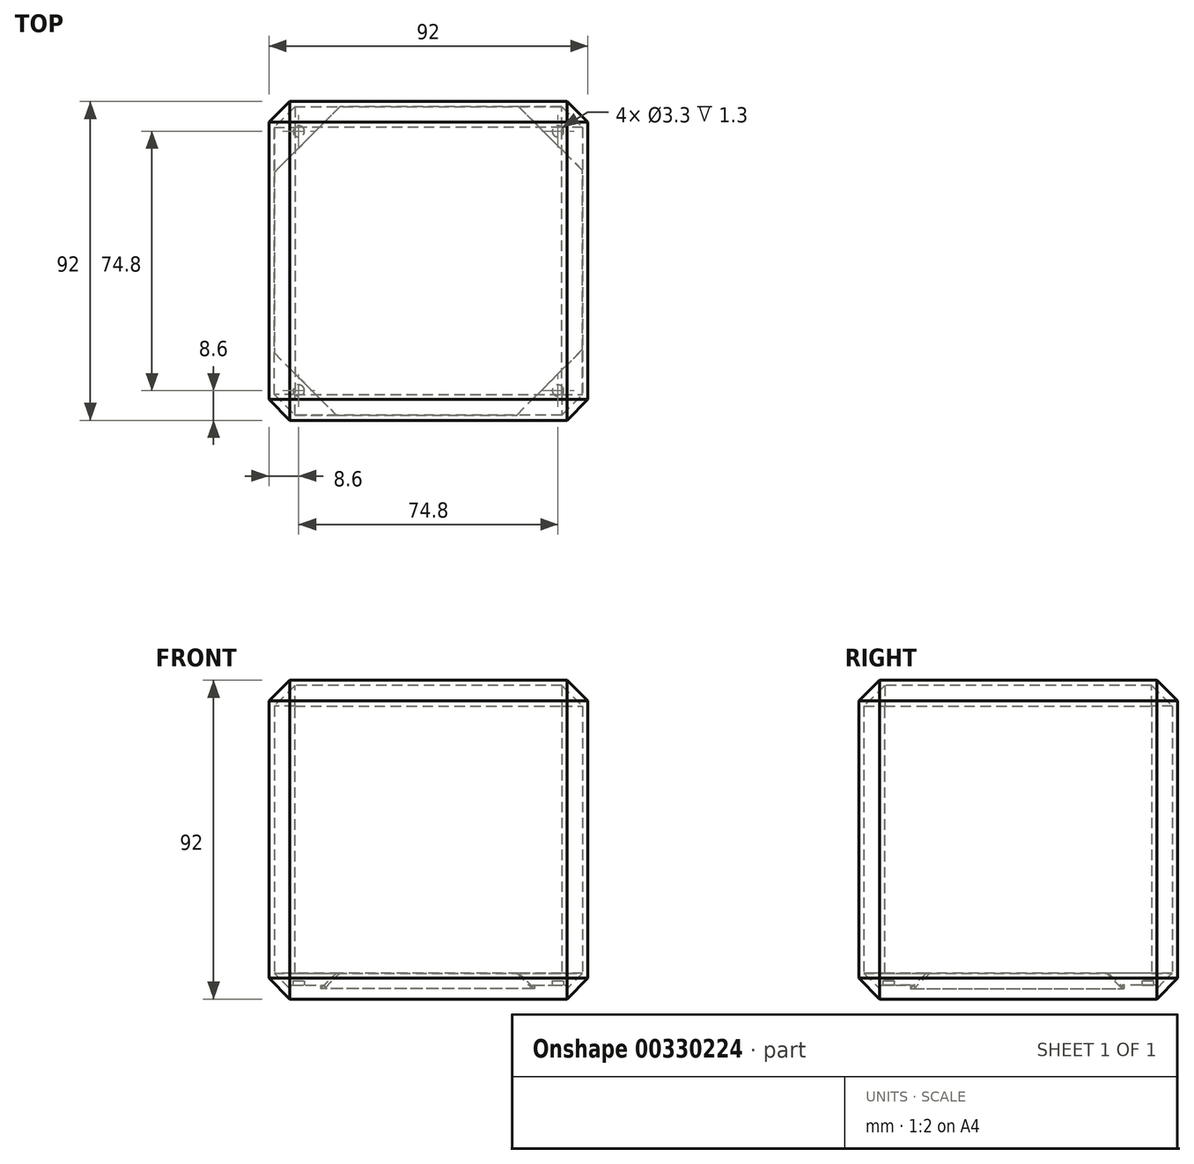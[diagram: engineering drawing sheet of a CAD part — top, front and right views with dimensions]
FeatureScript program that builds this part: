
annotation { "Feature Type Name" : "Feature", "Feature Type Description" : "" }
export const myFeature = defineFeature(function(context is Context, id is Id, definition is map)
    precondition{}
    {
        {
            var Q0;
            Q0=qCreatedBy(makeId("Top.planeOp"),FACE);
            var sketch = newSketch(context, id + "F0", { "sketchPlane" : qUnion([Q0])});
            skLineSegment(sketch, "E0.bottom", {"start": v(46, -46) * mm, "end": v(-46, -46) * mm});
            skLineSegment(sketch, "E0.top", {"start": v(46, 46) * mm, "end": v(-46, 46) * mm});
            skLineSegment(sketch, "E0.left", {"start": v(46, -46) * mm, "end": v(46, 46) * mm});
            skLineSegment(sketch, "E0.right", {"start": v(-46, -46) * mm, "end": v(-46, 46) * mm});
            skSolve(sketch);
        }
        {
            var Q0;
            Q0=qSketchRegion(id+"F0",true);
            extrude(context, id + "F1", {"entities" : qUnion([Q0]), "depth" : 92 * mm});
        }
        {
            var Q0;
            Q0=makeQuery(id+"F1.opExtrude","CAP_EDGE",EDGE,{"disambiguationData":[OSD([sQuery(id+"F0.wireOp",EDGE,"E0.bottom")])],"isStart":false});
            var Q1;
            Q1=makeQuery(id+"F1.opExtrude","CAP_EDGE",EDGE,{"disambiguationData":[OSD([sQuery(id+"F0.wireOp",EDGE,"E0.left")])],"isStart":false});
            var Q2;
            Q2=makeQuery(id+"F1.opExtrude","SWEPT_EDGE",EDGE,{"disambiguationData":[OSD([sQuery(id+"F0.wireOp",EDGE,"E0.bottom"),sQuery(id+"F0.wireOp",EDGE,"E0.left")])]});
            var Q3;
            Q3=makeQuery(id+"F1.opExtrude","CAP_EDGE",EDGE,{"disambiguationData":[OSD([sQuery(id+"F0.wireOp",EDGE,"E0.bottom")])],"isStart":true});
            var Q4;
            Q4=makeQuery(id+"F1.opExtrude","SWEPT_EDGE",EDGE,{"disambiguationData":[OSD([sQuery(id+"F0.wireOp",EDGE,"E0.bottom"),sQuery(id+"F0.wireOp",EDGE,"E0.right")])]});
            var Q5;
            Q5=makeQuery(id+"F1.opExtrude","CAP_EDGE",EDGE,{"disambiguationData":[OSD([sQuery(id+"F0.wireOp",EDGE,"E0.left")])],"isStart":true});
            var Q6;
            Q6=makeQuery(id+"F1.opExtrude","SWEPT_EDGE",EDGE,{"disambiguationData":[OSD([sQuery(id+"F0.wireOp",EDGE,"E0.top"),sQuery(id+"F0.wireOp",EDGE,"E0.left")])]});
            var Q7;
            Q7=makeQuery(id+"F1.opExtrude","CAP_EDGE",EDGE,{"disambiguationData":[OSD([sQuery(id+"F0.wireOp",EDGE,"E0.top")])],"isStart":false});
            var Q8;
            Q8=makeQuery(id+"F1.opExtrude","CAP_EDGE",EDGE,{"disambiguationData":[OSD([sQuery(id+"F0.wireOp",EDGE,"E0.right")])],"isStart":false});
            var Q9;
            Q9=makeQuery(id+"F1.opExtrude","CAP_EDGE",EDGE,{"disambiguationData":[OSD([sQuery(id+"F0.wireOp",EDGE,"E0.right")])],"isStart":true});
            var Q10;
            Q10=makeQuery(id+"F1.opExtrude","SWEPT_EDGE",EDGE,{"disambiguationData":[OSD([sQuery(id+"F0.wireOp",EDGE,"E0.top"),sQuery(id+"F0.wireOp",EDGE,"E0.right")])]});
            var Q11;
            Q11=makeQuery(id+"F1.opExtrude","CAP_EDGE",EDGE,{"disambiguationData":[OSD([sQuery(id+"F0.wireOp",EDGE,"E0.top")])],"isStart":true});
            chamfer(context, id + "F2", {"entities" : qUnion([Q0, Q1, Q2, Q3, Q4, Q5, Q6, Q7, Q8, Q9, Q10, Q11]), "width" : 6 * mm, "tangentPropagation" : true});
        }
        {
            var Q0;
            Q0=makeQuery(id+"F1.opExtrude","CAP_FACE",FACE,{"disambiguationData":[OSD([sQuery(id+"F0.wireOp",EDGE,"E0.bottom"),sQuery(id+"F0.wireOp",EDGE,"E0.top"),sQuery(id+"F0.wireOp",EDGE,"E0.left"),sQuery(id+"F0.wireOp",EDGE,"E0.right")])],"isStart":true});
            extrude(context, id + "F3", {"entities" : qUnion([Q0]), "operationType" : NewBodyOperationType.REMOVE, "oppositeDirection" : true, "depth" : 80 * mm});
        }
        {
            var Q0;
            Q0=qCreatedBy(makeId("Top.planeOp"),FACE);
            var sketch = newSketch(context, id + "F4", { "sketchPlane" : qUnion([Q0])});
            skLineSegment(sketch, "E1.bottom", {"start": v(-44.5, 44.5) * mm, "end": v(44.5, 44.5) * mm});
            skLineSegment(sketch, "E1.top", {"start": v(-44.5, -44.5) * mm, "end": v(44.5, -44.5) * mm});
            skLineSegment(sketch, "E1.left", {"start": v(-44.5, 44.5) * mm, "end": v(-44.5, -44.5) * mm});
            skLineSegment(sketch, "E1.right", {"start": v(44.5, 44.5) * mm, "end": v(44.5, -44.5) * mm});
            skSolve(sketch);
        }
        {
            var Q0;
            Q0=qSketchRegion(id+"F4",true);
            extrude(context, id + "F5", {"entities" : qUnion([Q0]), "depth" : 89 * mm});
        }
        {
            var Q0;
            Q0=makeQuery(id+"F5.opExtrude","SWEPT_EDGE",EDGE,{"disambiguationData":[OSD([sQuery(id+"F4.wireOp",EDGE,"E1.top"),sQuery(id+"F4.wireOp",EDGE,"E1.left")])]});
            var Q1;
            Q1=makeQuery(id+"F5.opExtrude","CAP_EDGE",EDGE,{"disambiguationData":[OSD([sQuery(id+"F4.wireOp",EDGE,"E1.top")])],"isStart":false});
            var Q2;
            Q2=makeQuery(id+"F5.opExtrude","SWEPT_EDGE",EDGE,{"disambiguationData":[OSD([sQuery(id+"F4.wireOp",EDGE,"E1.top"),sQuery(id+"F4.wireOp",EDGE,"E1.right")])]});
            var Q3;
            Q3=makeQuery(id+"F5.opExtrude","CAP_EDGE",EDGE,{"disambiguationData":[OSD([sQuery(id+"F4.wireOp",EDGE,"E1.top")])],"isStart":true});
            var Q4;
            Q4=makeQuery(id+"F5.opExtrude","CAP_EDGE",EDGE,{"disambiguationData":[OSD([sQuery(id+"F4.wireOp",EDGE,"E1.right")])],"isStart":false});
            var Q5;
            Q5=makeQuery(id+"F5.opExtrude","SWEPT_EDGE",EDGE,{"disambiguationData":[OSD([sQuery(id+"F4.wireOp",EDGE,"E1.bottom"),sQuery(id+"F4.wireOp",EDGE,"E1.right")])]});
            var Q6;
            Q6=makeQuery(id+"F5.opExtrude","CAP_EDGE",EDGE,{"disambiguationData":[OSD([sQuery(id+"F4.wireOp",EDGE,"E1.right")])],"isStart":true});
            var Q7;
            Q7=makeQuery(id+"F5.opExtrude","CAP_EDGE",EDGE,{"disambiguationData":[OSD([sQuery(id+"F4.wireOp",EDGE,"E1.bottom")])],"isStart":true});
            var Q8;
            Q8=makeQuery(id+"F5.opExtrude","CAP_EDGE",EDGE,{"disambiguationData":[OSD([sQuery(id+"F4.wireOp",EDGE,"E1.left")])],"isStart":false});
            var Q9;
            Q9=makeQuery(id+"F5.opExtrude","CAP_EDGE",EDGE,{"disambiguationData":[OSD([sQuery(id+"F4.wireOp",EDGE,"E1.bottom")])],"isStart":false});
            var Q10;
            Q10=makeQuery(id+"F5.opExtrude","SWEPT_EDGE",EDGE,{"disambiguationData":[OSD([sQuery(id+"F4.wireOp",EDGE,"E1.bottom"),sQuery(id+"F4.wireOp",EDGE,"E1.left")])]});
            var Q11;
            Q11=makeQuery(id+"F5.opExtrude","CAP_EDGE",EDGE,{"disambiguationData":[OSD([sQuery(id+"F4.wireOp",EDGE,"E1.left")])],"isStart":true});
            chamfer(context, id + "F6", {"entities" : qUnion([Q0, Q1, Q2, Q3, Q4, Q5, Q6, Q7, Q8, Q9, Q10, Q11]), "width" : 6 * mm, "tangentPropagation" : true});
        }
        {
            var Q0;
            Q0=makeQuery(id+"F5.opExtrude","SWEPT_BODY",BODY,{"disambiguationData":[OSD([sQuery(id+"F4.wireOp",EDGE,"E1.bottom"),sQuery(id+"F4.wireOp",EDGE,"E1.top"),sQuery(id+"F4.wireOp",EDGE,"E1.left"),sQuery(id+"F4.wireOp",EDGE,"E1.right")])]});
            transform(context, id + "F7", {"entities" : qUnion([Q0]), "transformType" : TransformType.TRANSLATION_3D, "dx" : 0 * mm, "dy" : 0 * mm, "dz" : 1.5 * mm, "makeCopy" : false});
        }
        {
            var Q0;
            Q0=makeQuery(id+"F5.opExtrude","SWEPT_BODY",BODY,{"disambiguationData":[OSD([sQuery(id+"F4.wireOp",EDGE,"E1.bottom"),sQuery(id+"F4.wireOp",EDGE,"E1.top"),sQuery(id+"F4.wireOp",EDGE,"E1.left"),sQuery(id+"F4.wireOp",EDGE,"E1.right")])]});
            var Q1;
            Q1=makeQuery(id+"F1.opExtrude","SWEPT_BODY",BODY,{"disambiguationData":[OSD([sQuery(id+"F0.wireOp",EDGE,"E0.bottom"),sQuery(id+"F0.wireOp",EDGE,"E0.top"),sQuery(id+"F0.wireOp",EDGE,"E0.left"),sQuery(id+"F0.wireOp",EDGE,"E0.right")])]});
            booleanBodies(context, id + "F8", {"operationType" : BooleanOperationType.SUBTRACTION, "tools" : qUnion([Q0]), "targets" : qUnion([Q1])});
        }
        {
            var Q0;
            Q0=qCreatedBy(makeId("Top.planeOp"),FACE);
            cPlane(context, id + "F9", {"entities" : qUnion([Q0]), "cplaneType" : CPlaneType.OFFSET, "offset" : 7.5 * mm, "width" : 150 * mm, "height" : 150 * mm});
        }
        {
            var Q0;
            Q0=qCreatedBy(id+"F9.planeOp",FACE);
            var sketch = newSketch(context, id + "F16", { "sketchPlane" : qUnion([Q0])});
            skLineSegment(sketch, "E2.0", {"start": v(44.5, 38.5) * mm, "end": v(44.5, 26.07) * mm});
            skLineSegment(sketch, "E2.1", {"start": v(38.5, 44.5) * mm, "end": v(44.5, 38.5) * mm});
            skLineSegment(sketch, "E2.2", {"start": v(-38.5, 44.5) * mm, "end": v(-25.5, 44.5) * mm});
            skLineSegment(sketch, "E2.3", {"start": v(38.5, -44.5) * mm, "end": v(25.5, -44.5) * mm});
            skLineSegment(sketch, "E2.4", {"start": v(44.5, -38.5) * mm, "end": v(38.5, -44.5) * mm});
            skLineSegment(sketch, "E2.5", {"start": v(-38.5, -44.5) * mm, "end": v(-44.5, -38.5) * mm});
            skLineSegment(sketch, "E2.6", {"start": v(-44.5, -38.5) * mm, "end": v(-44.5, -26.54) * mm});
            skLineSegment(sketch, "E2.7", {"start": v(-44.5, 38.5) * mm, "end": v(-38.5, 44.5) * mm});
            skPoint(sketch, "E3.0.end.orphan", {"position": v(40, 40) * mm});
            skPoint(sketch, "E4.0.end.orphan", {"position": v(-40, 40) * mm});
            skPoint(sketch, "E5.0.end.orphan", {"position": v(-40, -40) * mm});
            skPoint(sketch, "E5.0.start.orphan", {"position": v(40, -40) * mm});
            skLineSegment(sketch, "E6", {"start": v(30, -40) * mm, "end": v(40, -30) * mm});
            skLineSegment(sketch, "E7.MirrorCS", {"start": v(-30, -41.04) * mm, "end": v(-40, -31.04) * mm});
            skLineSegment(sketch, "E8.MirrorCS", {"start": v(30.57, 40) * mm, "end": v(40.57, 30) * mm});
            skLineSegment(sketch, "E9.MirrorCS", {"start": v(-30, 40) * mm, "end": v(-40, 30) * mm});
            skLineSegment(sketch, "E10", {"start": v(40, -30) * mm, "end": v(44.5, -25.5) * mm});
            skLineSegment(sketch, "E11", {"start": v(30, -40) * mm, "end": v(25.5, -44.5) * mm});
            skLineSegment(sketch, "E12", {"start": v(-30, -41.04) * mm, "end": v(-26.54, -44.5) * mm});
            skLineSegment(sketch, "E13", {"start": v(-40, -31.04) * mm, "end": v(-44.5, -26.54) * mm});
            skLineSegment(sketch, "E14", {"start": v(-40, 30) * mm, "end": v(-44.5, 25.5) * mm});
            skLineSegment(sketch, "E15", {"start": v(-30, 40) * mm, "end": v(-25.5, 44.5) * mm});
            skLineSegment(sketch, "E16", {"start": v(30.57, 40) * mm, "end": v(26.07, 44.5) * mm});
            skLineSegment(sketch, "E17", {"start": v(40.57, 30) * mm, "end": v(44.5, 26.07) * mm});
            skLineSegment(sketch, "E18.trimOffspring", {"start": v(44.5, -25.5) * mm, "end": v(44.5, -38.5) * mm});
            skLineSegment(sketch, "E19.trimOffspring", {"start": v(26.07, 44.5) * mm, "end": v(38.5, 44.5) * mm});
            skLineSegment(sketch, "E20.trimOffspring", {"start": v(-44.5, 25.5) * mm, "end": v(-44.5, 38.5) * mm});
            skLineSegment(sketch, "E21.trimOffspring", {"start": v(-26.54, -44.5) * mm, "end": v(-38.5, -44.5) * mm});
            skSolve(sketch);
        }
        {
            var Q0;
            Q0=qSketchRegion(id+"F16",true);
            extrude(context, id + "F17", {"entities" : qUnion([Q0]), "operationType" : NewBodyOperationType.ADD, "oppositeDirection" : true, "depth" : 3.5 * mm});
        }
        {
            var Q0;
            Q0=makeQuery(id+"F17.opExtrude","CAP_FACE",FACE,{"disambiguationData":[OSD([sQuery(id+"F16.wireOp",EDGE,"E2.5"),sQuery(id+"F16.wireOp",EDGE,"E2.6"),sQuery(id+"F16.wireOp",EDGE,"E7.MirrorCS"),sQuery(id+"F16.wireOp",EDGE,"E12"),sQuery(id+"F16.wireOp",EDGE,"E13"),sQuery(id+"F16.wireOp",EDGE,"E21.trimOffspring")])],"isStart":false});
            var sketch = newSketch(context, id + "F10", { "sketchPlane" : qUnion([Q0])});
            skCircle(sketch, "E22", {"center": v(37.4, 37.4) * mm, "radius": 1.65 * mm});
            skCircle(sketch, "E23.MirrorC", {"center": v(-37.4, 37.4) * mm, "radius": 1.65 * mm});
            skCircle(sketch, "E24.MirrorC", {"center": v(-37.4, -37.4) * mm, "radius": 1.65 * mm});
            skCircle(sketch, "E25.MirrorC", {"center": v(37.4, -37.4) * mm, "radius": 1.65 * mm});
            skSolve(sketch);
        }
        {
            var Q0;
            Q0=qSketchRegion(id+"F10",true);
            extrude(context, id + "F11", {"entities" : qUnion([Q0]), "operationType" : NewBodyOperationType.REMOVE, "oppositeDirection" : true, "depth" : 1.3 * mm});
        }
        {
            var Q0;
            Q0=makeQuery(id+"F17.opExtrude","CAP_EDGE",EDGE,{"disambiguationData":[OSD([sQuery(id+"F16.wireOp",EDGE,"E2.2")])],"isStart":false});
            var Q1;
            Q1=makeQuery(id+"F17.opExtrude","CAP_EDGE",EDGE,{"disambiguationData":[OSD([sQuery(id+"F16.wireOp",EDGE,"E20.trimOffspring")])],"isStart":false});
            var Q2;
            Q2=makeQuery(id+"F17.opExtrude","CAP_EDGE",EDGE,{"disambiguationData":[OSD([sQuery(id+"F16.wireOp",EDGE,"E19.trimOffspring")])],"isStart":false});
            var Q3;
            Q3=makeQuery(id+"F17.opExtrude","CAP_EDGE",EDGE,{"disambiguationData":[OSD([sQuery(id+"F16.wireOp",EDGE,"E2.0")])],"isStart":false});
            var Q4;
            Q4=makeQuery(id+"F17.opExtrude","CAP_EDGE",EDGE,{"disambiguationData":[OSD([sQuery(id+"F16.wireOp",EDGE,"E18.trimOffspring")])],"isStart":false});
            var Q5;
            Q5=makeQuery(id+"F17.opExtrude","CAP_EDGE",EDGE,{"disambiguationData":[OSD([sQuery(id+"F16.wireOp",EDGE,"E21.trimOffspring")])],"isStart":false});
            var Q6;
            Q6=makeQuery(id+"F17.opExtrude","CAP_EDGE",EDGE,{"disambiguationData":[OSD([sQuery(id+"F16.wireOp",EDGE,"E2.6")])],"isStart":false});
            var Q7;
            Q7=makeQuery(id+"F17.opExtrude","CAP_EDGE",EDGE,{"disambiguationData":[OSD([sQuery(id+"F16.wireOp",EDGE,"E2.3")])],"isStart":false});
            chamfer(context, id + "F12", {"entities" : qUnion([Q0, Q1, Q2, Q3, Q4, Q5, Q6, Q7]), "width" : 0.5 * mm, "tangentPropagation" : true});
        }
        {
            var Q0;
            {var subQ0=sQuery(id+"F4.wireOp",EDGE,"E1.top");var subQ1=sQuery(id+"F0.wireOp",EDGE,"E0.right");var subQ2=sQuery(id+"F0.wireOp",EDGE,"E0.left");var subQ3=sQuery(id+"F0.wireOp",EDGE,"E0.top");var subQ4=sQuery(id+"F0.wireOp",EDGE,"E0.bottom");Q0=makeQuery(id+"F8.opBoolean","INTERSECT",EDGE,{"derivedFrom":[makeQuery(id+"F3.boolean.opBoolean","COPY",FACE,{"derivedFrom":makeQuery(id+"F3.opExtrude","SWEPT_FACE",FACE,{"disambiguationData":[OSD([subQ4,subQ3,subQ2,subQ1]),TDD([makeQuery(id+"F2.opChamfer","BLEND_EDGE",EDGE,{"blendedFrom":[makeQuery(id+"F1.opExtrude","CAP_EDGE",EDGE,{"disambiguationData":[OSD([subQ4])],"isStart":true}),makeQuery(id+"F1.opExtrude","CAP_FACE",FACE,{"disambiguationData":[OSD([subQ4,subQ3,subQ2,subQ1])],"isStart":true})],"blendedInto":[makeQuery(id+"F1.opExtrude","CAP_FACE",FACE,{"disambiguationData":[OSD([subQ4,subQ3,subQ2,subQ1])],"isStart":true})]})])]})}),makeQuery(id+"F6.opChamfer","BLEND_FACE",FACE,{"disambiguationData":[OSD([subQ0]),TDD([makeQuery(id+"F5.opExtrude","CAP_EDGE",EDGE,{"disambiguationData":[OSD([subQ0])],"isStart":true})])]})]});}
            var Q1;
            {var subQ0=sQuery(id+"F4.wireOp",EDGE,"E1.bottom");var subQ1=sQuery(id+"F0.wireOp",EDGE,"E0.right");var subQ2=sQuery(id+"F0.wireOp",EDGE,"E0.left");var subQ3=sQuery(id+"F0.wireOp",EDGE,"E0.top");var subQ4=sQuery(id+"F0.wireOp",EDGE,"E0.bottom");Q1=makeQuery(id+"F8.opBoolean","INTERSECT",EDGE,{"derivedFrom":[makeQuery(id+"F3.boolean.opBoolean","COPY",FACE,{"derivedFrom":makeQuery(id+"F3.opExtrude","SWEPT_FACE",FACE,{"disambiguationData":[OSD([subQ4,subQ3,subQ2,subQ1]),TDD([makeQuery(id+"F2.opChamfer","BLEND_EDGE",EDGE,{"blendedFrom":[makeQuery(id+"F1.opExtrude","CAP_EDGE",EDGE,{"disambiguationData":[OSD([subQ3])],"isStart":true}),makeQuery(id+"F1.opExtrude","CAP_FACE",FACE,{"disambiguationData":[OSD([subQ4,subQ3,subQ2,subQ1])],"isStart":true})],"blendedInto":[makeQuery(id+"F1.opExtrude","CAP_FACE",FACE,{"disambiguationData":[OSD([subQ4,subQ3,subQ2,subQ1])],"isStart":true})]})])]})}),makeQuery(id+"F6.opChamfer","BLEND_FACE",FACE,{"disambiguationData":[OSD([subQ0]),TDD([makeQuery(id+"F5.opExtrude","CAP_EDGE",EDGE,{"disambiguationData":[OSD([subQ0])],"isStart":true})])]})]});}
            cPlane(context, id + "F13", {"entities" : qUnion([Q0, Q1]), "cplaneType" : CPlaneType.LINE_ANGLE, "offset" : 25 * mm, "angle" : 0 * degree, "width" : 150 * mm, "height" : 150 * mm});
        }
        {
            var Q0;
            Q0=qCreatedBy(id+"F13.planeOp",FACE);
            var sketch = newSketch(context, id + "F14", { "sketchPlane" : qUnion([Q0])});
            skLineSegment(sketch, "E26.0.0", {"start": v(-41, 30.04) * mm, "end": v(-40, 31.04) * mm});
            skLineSegment(sketch, "E26.0.1", {"start": v(-30.04, 41) * mm, "end": v(-38.5, 41) * mm});
            skLineSegment(sketch, "E26.0.3", {"start": v(-39.5, 40) * mm, "end": v(-40, 40) * mm});
            skLineSegment(sketch, "E26.0.4", {"start": v(-40, 40) * mm, "end": v(-40, 39.5) * mm});
            skLineSegment(sketch, "E26.0.6", {"start": v(-41, 38.5) * mm, "end": v(-41, 30.04) * mm});
            skLineSegment(sketch, "E26.1.0", {"start": v(29, 41) * mm, "end": v(30, 40) * mm});
            skLineSegment(sketch, "E26.1.1", {"start": v(41, 29) * mm, "end": v(41, 38.5) * mm});
            skLineSegment(sketch, "E26.1.3", {"start": v(40, 39.5) * mm, "end": v(40, 40) * mm});
            skLineSegment(sketch, "E26.1.4", {"start": v(40, 40) * mm, "end": v(39.5, 40) * mm});
            skLineSegment(sketch, "E26.1.6", {"start": v(38.5, 41) * mm, "end": v(29, 41) * mm});
            skLineSegment(sketch, "E26.2.0", {"start": v(41, -29.57) * mm, "end": v(40, -30.57) * mm});
            skLineSegment(sketch, "E26.2.1", {"start": v(29.57, -41) * mm, "end": v(38.5, -41) * mm});
            skLineSegment(sketch, "E26.2.6", {"start": v(41, -38.5) * mm, "end": v(41, -29.57) * mm});
            skLineSegment(sketch, "E26.3.0", {"start": v(-29, -41) * mm, "end": v(-30, -40) * mm});
            skLineSegment(sketch, "E26.3.1", {"start": v(-41, -29) * mm, "end": v(-41, -38.5) * mm});
            skLineSegment(sketch, "E26.3.6", {"start": v(-38.5, -41) * mm, "end": v(-29, -41) * mm});
            skLineSegment(sketch, "E27.0", {"start": v(-40, 40) * mm, "end": v(-40, 31.04) * mm});
            skLineSegment(sketch, "E27.1", {"start": v(40, 40) * mm, "end": v(30, 40) * mm});
            skLineSegment(sketch, "E27.2", {"start": v(40, -40) * mm, "end": v(40, -30.57) * mm});
            skLineSegment(sketch, "E27.3", {"start": v(-40, -40) * mm, "end": v(-30, -40) * mm});
            skLineSegment(sketch, "E28.trimOffspring", {"start": v(-31.04, 40) * mm, "end": v(-40, 40) * mm});
            skLineSegment(sketch, "E29.trimOffspring", {"start": v(-40, -30) * mm, "end": v(-40, -40) * mm});
            skLineSegment(sketch, "E30.trimOffspring", {"start": v(40, 30) * mm, "end": v(40, 40) * mm});
            skLineSegment(sketch, "E31.trimOffspring", {"start": v(40, 30) * mm, "end": v(41, 29) * mm});
            skLineSegment(sketch, "E32.trimOffspring", {"start": v(-31.04, 40) * mm, "end": v(-30.04, 41) * mm});
            skLineSegment(sketch, "E33", {"start": v(40, -30.57) * mm, "end": v(40, -40) * mm});
            skLineSegment(sketch, "E34", {"start": v(30.57, -40) * mm, "end": v(29.57, -41) * mm});
            skLineSegment(sketch, "E35", {"start": v(30.57, -40) * mm, "end": v(40, -40) * mm});
            skLineSegment(sketch, "E36", {"start": v(-41, -38.5) * mm, "end": v(-41, -40) * mm});
            skLineSegment(sketch, "E37", {"start": v(-41, -40) * mm, "end": v(-40, -41) * mm});
            skLineSegment(sketch, "E38", {"start": v(-40, -41) * mm, "end": v(-38.5, -41) * mm});
            skPoint(sketch, "E26.3.4.start.orphan", {"position": v(-40, -40) * mm});
            skPoint(sketch, "E26.3.5.start.orphan", {"position": v(-39.5, -40) * mm});
            skPoint(sketch, "E26.3.2.end.orphan", {"position": v(-40, -39.5) * mm});
            skLineSegment(sketch, "E39.trimOffspring", {"start": v(-40, -30) * mm, "end": v(-41, -29) * mm});
            skLineSegment(sketch, "E40", {"start": v(-41, 38.5) * mm, "end": v(-41, 40) * mm});
            skLineSegment(sketch, "E41", {"start": v(-41, 40) * mm, "end": v(-40, 41) * mm});
            skLineSegment(sketch, "E42", {"start": v(-40, 41) * mm, "end": v(-38.5, 41) * mm});
            skLineSegment(sketch, "E43", {"start": v(38.5, 41) * mm, "end": v(40, 41) * mm});
            skLineSegment(sketch, "E44", {"start": v(40, 41) * mm, "end": v(41, 40) * mm});
            skLineSegment(sketch, "E45", {"start": v(41, 40) * mm, "end": v(41, 38.5) * mm});
            skLineSegment(sketch, "E46", {"start": v(38.5, -41) * mm, "end": v(40, -41) * mm});
            skLineSegment(sketch, "E47", {"start": v(40, -41) * mm, "end": v(41, -40) * mm});
            skLineSegment(sketch, "E48", {"start": v(41, -40) * mm, "end": v(41, -38.5) * mm});
            skSolve(sketch);
        }
        {
            var Q0;
            Q0=qSketchRegion(id+"F14",true);
            extrude(context, id + "F15", {"entities" : qUnion([Q0]), "operationType" : NewBodyOperationType.ADD, "oppositeDirection" : true, "depth" : 1.5 * mm});
        }
    });
